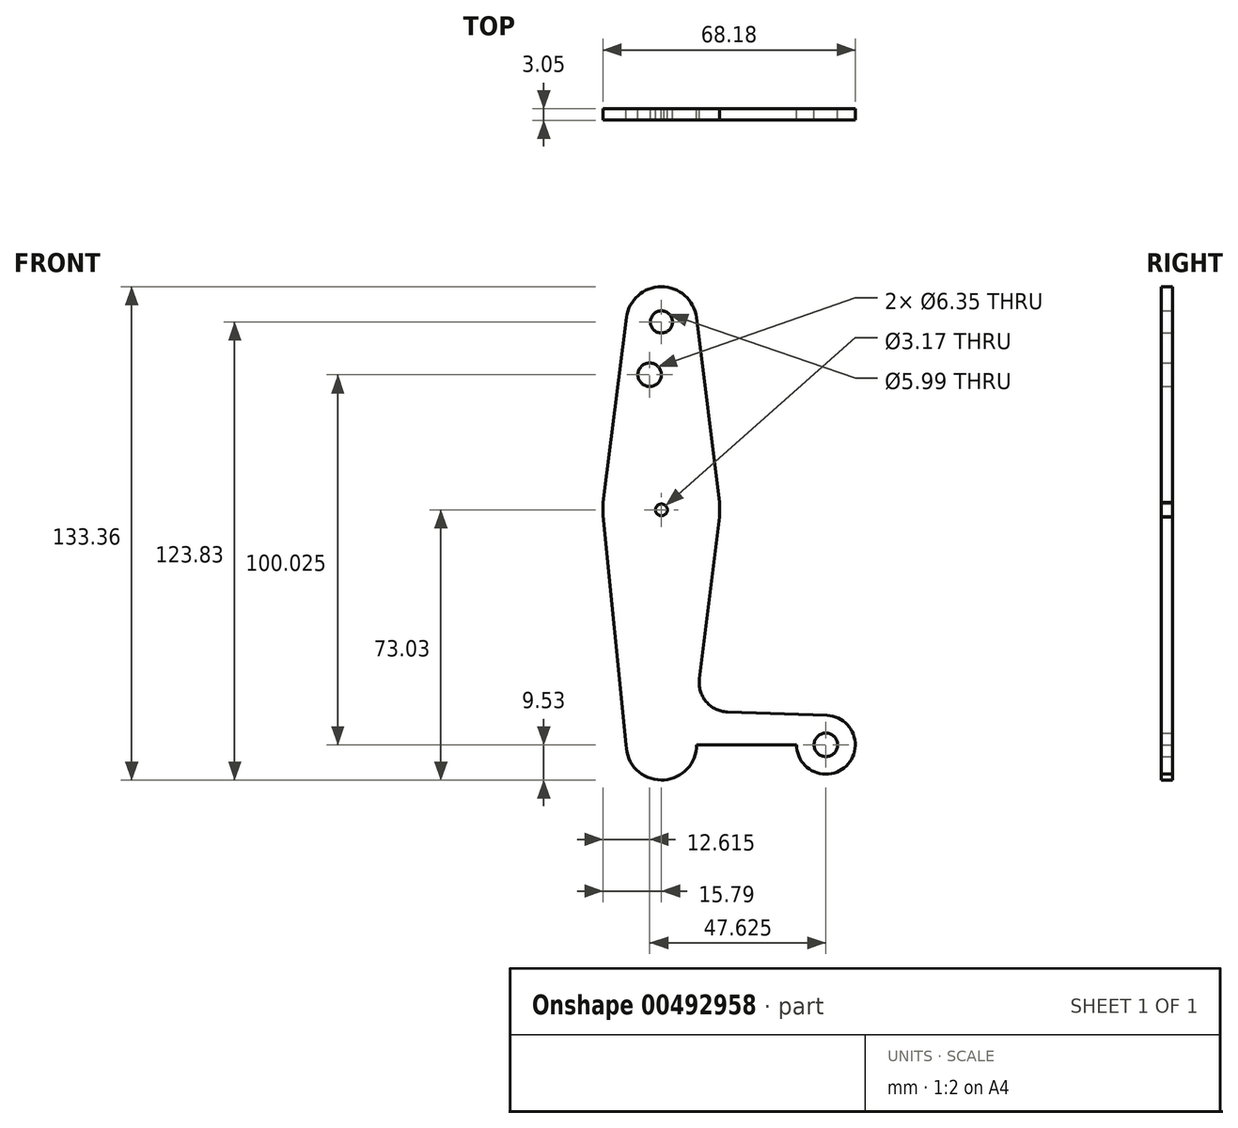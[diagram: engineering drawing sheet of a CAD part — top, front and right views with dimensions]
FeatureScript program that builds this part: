
annotation { "Feature Type Name" : "Feature", "Feature Type Description" : "" }
export const myFeature = defineFeature(function(context is Context, id is Id, definition is map)
    precondition{}
    {
        {
            var Q0;
            Q0=qCreatedBy(makeId("Front.planeOp"),FACE);
            var sketch = newSketch(context, id + "F0", { "sketchPlane" : qUnion([Q0])});
            skCircle(sketch, "E0", {"center": v(0, 114.3) * mm, "radius": 9.53 * mm});
            skCircle(sketch, "E1", {"center": v(0, 63.5) * mm, "radius": 15.88 * mm});
            skCircle(sketch, "E2", {"center": v(0, 0) * mm, "radius": 9.53 * mm});
            skCircle(sketch, "E3", {"center": v(44.45, 0) * mm, "radius": 7.94 * mm});
            skLineSegment(sketch, "E4", {"start": v(0, 0) * mm, "end": v(0, 114.3) * mm});
            skLineSegment(sketch, "E5", {"start": v(0, 0) * mm, "end": v(44.45, 0) * mm});
            skLineSegment(sketch, "E6", {"start": v(-9.45, 115.5) * mm, "end": v(-15.75, 65.48) * mm});
            skLineSegment(sketch, "E7", {"start": v(9.45, 115.5) * mm, "end": v(15.75, 65.48) * mm});
            skLineSegment(sketch, "E8", {"start": v(17.85, 8.89) * mm, "end": v(44.73, 7.93) * mm});
            skLineSegment(sketch, "E9", {"start": v(0, -9.53) * mm, "end": v(44.73, -7.93) * mm});
            skLineSegment(sketch, "E10", {"start": v(15.75, 65.48) * mm, "end": v(15.75, 61.52) * mm});
            skLineSegment(sketch, "E11", {"start": v(15.75, 61.52) * mm, "end": v(10.25, 17.83) * mm});
            skLineSegment(sketch, "E12", {"start": v(-15.75, 65.48) * mm, "end": v(-15.8, 61.9) * mm});
            skLineSegment(sketch, "E13", {"start": v(-15.8, 61.9) * mm, "end": v(-9.52, 0) * mm});
            skCircle(sketch, "E14", {"center": v(0, 63.5) * mm, "radius": 1.59 * mm});
            skCircle(sketch, "E15", {"center": v(-3.18, 100.03) * mm, "radius": 3.18 * mm});
            skCircle(sketch, "E16", {"center": v(0, 114.3) * mm, "radius": 3 * mm});
            skCircle(sketch, "E17", {"center": v(44.45, 0) * mm, "radius": 3.18 * mm});
            skArc(sketch, "E18.filletArc", {"start": v(10.25, 17.83) * mm, "mid": v(12.08, 11.68) * mm, "end": v(17.85, 8.89) * mm});
            skSolve(sketch);
        }
        {
            var Q0;
            Q0=makeQuery(id+"F0.imprint","IMPRINT",FACE,{"disambiguationData":[TD([[makeQuery(id+"F0.imprint","IMPRINT",EDGE,{"derivedFrom":sQuery(id+"F0.wireOp",EDGE,"E16")}),-1.0]])]});
            var Q1;
            {var subQ6=sQuery(id+"F0.wireOp",EDGE,"E7");Q1=makeQuery(id+"F0.imprint","IMPRINT",FACE,{"disambiguationData":[TD([[makeQuery(id+"F0.imprint","IMPRINT",EDGE,{"derivedFrom":subQ6}),-1.0]])]});}
            var Q2;
            {var subQ5=sQuery(id+"F0.wireOp",EDGE,"E10");Q2=makeQuery(id+"F0.imprint","IMPRINT",FACE,{"disambiguationData":[TD([[makeQuery(id+"F0.imprint","IMPRINT",EDGE,{"derivedFrom":subQ5}),-1.0]])]});}
            var Q3;
            {var subQ7=sQuery(id+"F0.wireOp",EDGE,"E12");Q3=makeQuery(id+"F0.imprint","IMPRINT",FACE,{"disambiguationData":[TD([[makeQuery(id+"F0.imprint","IMPRINT",EDGE,{"derivedFrom":subQ7}),1.0]])]});}
            var Q4;
            {var subQ7=sQuery(id+"F0.wireOp",EDGE,"E6");Q4=makeQuery(id+"F0.imprint","IMPRINT",FACE,{"disambiguationData":[TD([[makeQuery(id+"F0.imprint","IMPRINT",EDGE,{"derivedFrom":subQ7}),1.0]])]});}
            var Q5;
            {var subQ0=sQuery(id+"F0.wireOp",EDGE,"E13");Q5=makeQuery(id+"F0.imprint","IMPRINT",FACE,{"disambiguationData":[TD([[makeQuery(id+"F0.imprint","IMPRINT",EDGE,{"derivedFrom":subQ0}),1.0]])]});}
            var Q6;
            {var subQ10=sQuery(id+"F0.wireOp",EDGE,"E8");Q6=makeQuery(id+"F0.imprint","IMPRINT",FACE,{"disambiguationData":[TD([[makeQuery(id+"F0.imprint","IMPRINT",EDGE,{"derivedFrom":subQ10}),-1.0]])]});}
            var Q7;
            {var subQ3=sQuery(id+"F0.wireOp",EDGE,"E2");var subQ9=makeQuery(id+"F0.imprint","INTERSECT",VERTEX,{"derivedFrom":[subQ3,sQuery(id+"F0.wireOp",EDGE,"E13")]});Q7=makeQuery(id+"F0.imprint","IMPRINT",FACE,{"disambiguationData":[TD([[makeQuery(id+"F0.imprint","IMPRINT",EDGE,{"disambiguationData":[TD([[subQ9,1.0]])],"derivedFrom":subQ3}),1.0]])]});}
            var Q8;
            {var subQ0=sQuery(id+"F0.wireOp",EDGE,"E9");var subQ1=sQuery(id+"F0.wireOp",EDGE,"E2");var subQ2=makeQuery(id+"F0.imprint","INTERSECT",VERTEX,{"disambiguationData":[OD(1.0)],"derivedFrom":[subQ1,subQ0]});Q8=makeQuery(id+"F0.imprint","IMPRINT",FACE,{"disambiguationData":[TD([[makeQuery(id+"F0.imprint","IMPRINT",EDGE,{"disambiguationData":[TD([[subQ2,-1.0]])],"derivedFrom":subQ1}),-1.0]])]});}
            var Q9;
            {var subQ0=sQuery(id+"F0.wireOp",EDGE,"E4");var subQ1=sQuery(id+"F0.wireOp",EDGE,"E2");var subQ2=makeQuery(id+"F0.imprint","INTERSECT",VERTEX,{"derivedFrom":[subQ1,subQ0]});Q9=makeQuery(id+"F0.imprint","IMPRINT",FACE,{"disambiguationData":[TD([[makeQuery(id+"F0.imprint","IMPRINT",EDGE,{"disambiguationData":[TD([[subQ2,1.0]])],"derivedFrom":subQ1}),1.0]])]});}
            var Q10;
            Q10=makeQuery(id+"F0.imprint","IMPRINT",FACE,{"disambiguationData":[TD([[makeQuery(id+"F0.imprint","IMPRINT",EDGE,{"derivedFrom":sQuery(id+"F0.wireOp",EDGE,"E17")}),-1.0]])]});
            extrude(context, id + "F1", {"entities" : qUnion([Q0, Q1, Q2, Q3, Q4, Q5, Q6, Q7, Q8, Q9, Q10]), "depth" : 3.05 * mm});
        }
    });
